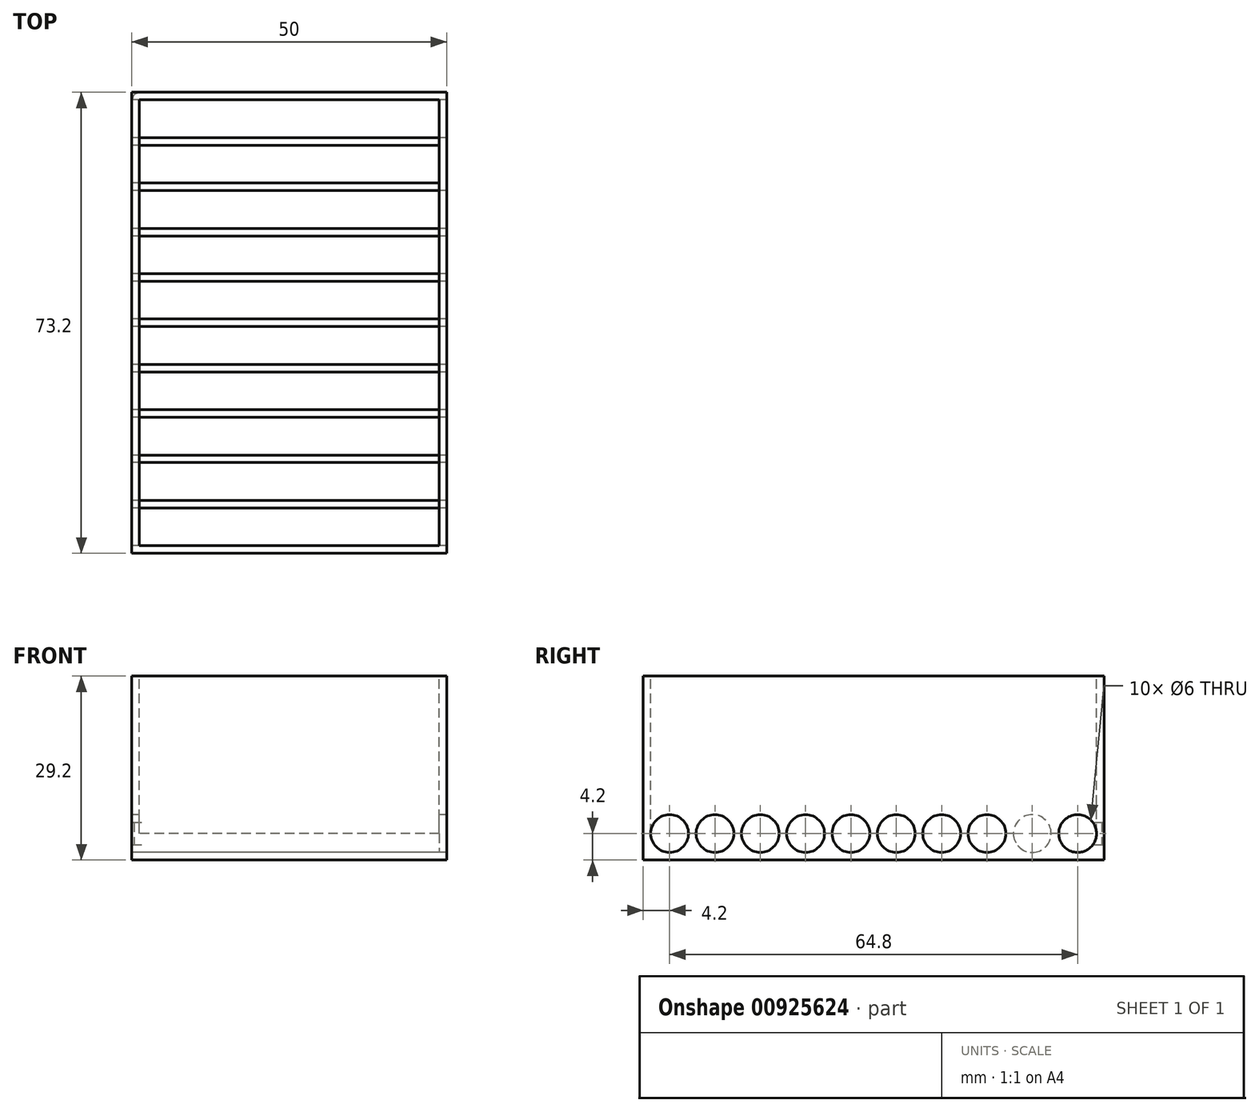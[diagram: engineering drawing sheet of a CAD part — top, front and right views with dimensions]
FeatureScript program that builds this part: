
annotation { "Feature Type Name" : "Feature", "Feature Type Description" : "" }
export const myFeature = defineFeature(function(context is Context, id is Id, definition is map)
    precondition{}
    {
        {
            assignVariable(context, id + "F0", {"name" : "FuseLength", "anyValue" : 20});
        }
        {
            var Q0;
            Q0=qCreatedBy(makeId("Right.planeOp"),FACE);
            var sketch = newSketch(context, id + "F1", { "sketchPlane" : qUnion([Q0])});
            skCircle(sketch, "E0", {"center": v(0, 3) * mm, "radius": 3 * mm});
            skCircle(sketch, "E1.1.0.0", {"center": v(7.2, 3) * mm, "radius": 3 * mm});
            skCircle(sketch, "E1.2.0.0", {"center": v(14.4, 3) * mm, "radius": 3 * mm});
            skCircle(sketch, "E1.3.0.0", {"center": v(21.6, 3) * mm, "radius": 3 * mm});
            skCircle(sketch, "E1.4.0.0", {"center": v(28.8, 3) * mm, "radius": 3 * mm});
            skCircle(sketch, "E1.5.0.0", {"center": v(36, 3) * mm, "radius": 3 * mm});
            skCircle(sketch, "E1.6.0.0", {"center": v(43.2, 3) * mm, "radius": 3 * mm});
            skCircle(sketch, "E1.7.0.0", {"center": v(50.4, 3) * mm, "radius": 3 * mm});
            skCircle(sketch, "E1.8.0.0", {"center": v(57.6, 3) * mm, "radius": 3 * mm});
            skCircle(sketch, "E1.9.0.0", {"center": v(64.8, 3) * mm, "radius": 3 * mm});
            skLineSegment(sketch, "E1.direction1", {"start": v(0, 3) * mm, "end": v(7.2, 3) * mm, "construction": true});
            skLineSegment(sketch, "E2", {"start": v(69, 3) * mm, "end": v(-4.2, 3) * mm});
            skLineSegment(sketch, "E3", {"start": v(-4.2, 3) * mm, "end": v(-4.2, -1.2) * mm});
            skLineSegment(sketch, "E4", {"start": v(-4.2, -1.2) * mm, "end": v(69, -1.2) * mm});
            skLineSegment(sketch, "E5", {"start": v(69, -1.2) * mm, "end": v(69, 3) * mm});
            skLineSegment(sketch, "E6.top", {"start": v(69, 28) * mm, "end": v(-4.2, 28) * mm});
            skLineSegment(sketch, "E6.left", {"start": v(69, 3) * mm, "end": v(69, 28) * mm});
            skLineSegment(sketch, "E6.right", {"start": v(-4.2, 3) * mm, "end": v(-4.2, 28) * mm});
            skSolve(sketch);
        }
        {
            var Q0;
            {var subQ0=sQuery(id+"F1.wireOp",EDGE,"E3");Q0=makeQuery(id+"F1.imprint","IMPRINT",FACE,{"disambiguationData":[TD([[makeQuery(id+"F1.imprint","IMPRINT",EDGE,{"derivedFrom":subQ0}),1.0]])]});}
            extrude(context, id + "F2", {"entities" : qUnion([Q0]), "depth" : (getVariable(context, 'FuseLength') * 2.5) * mm, "offsetDistance" : 25 * mm});
        }
        {
            var Q0;
            Q0=makeQuery(id+"F1.imprint","IMPRINT",FACE,{"disambiguationData":[TD([[makeQuery(id+"F1.imprint","IMPRINT",EDGE,{"derivedFrom":sQuery(id+"F1.wireOp",EDGE,"E6.top")}),1.0]])]});
            extrude(context, id + "F3", {"entities" : qUnion([Q0]), "operationType" : NewBodyOperationType.ADD, "depth" : 1.2 * mm, "offsetDistance" : 25 * mm});
        }
        {
            var Q0;
            Q0=makeQuery(id+"F2.opExtrude","CAP_FACE",FACE,{"disambiguationData":[OSD([sQuery(id+"F1.wireOp",EDGE,"E0"),sQuery(id+"F1.wireOp",EDGE,"E1.1.0.0"),sQuery(id+"F1.wireOp",EDGE,"E1.2.0.0"),sQuery(id+"F1.wireOp",EDGE,"E1.3.0.0"),sQuery(id+"F1.wireOp",EDGE,"E1.4.0.0"),sQuery(id+"F1.wireOp",EDGE,"E1.5.0.0"),sQuery(id+"F1.wireOp",EDGE,"E1.6.0.0"),sQuery(id+"F1.wireOp",EDGE,"E1.7.0.0"),sQuery(id+"F1.wireOp",EDGE,"E1.8.0.0"),sQuery(id+"F1.wireOp",EDGE,"E1.9.0.0"),sQuery(id+"F1.wireOp",EDGE,"E3"),sQuery(id+"F1.wireOp",EDGE,"E4"),sQuery(id+"F1.wireOp",EDGE,"E5"),sQuery(id+"F1.wireOp",EDGE,"E2")])],"isStart":false});
            var sketch = newSketch(context, id + "F4", { "sketchPlane" : qUnion([Q0])});
            skArc(sketch, "E7.0.0", {"start": v(54.6, 3) * mm, "mid": v(57.6, 6) * mm, "end": v(60.6, 3) * mm});
            skLineSegment(sketch, "E7.0.1", {"start": v(60.6, 3) * mm, "end": v(61.8, 3) * mm});
            skArc(sketch, "E7.0.2", {"start": v(61.8, 3) * mm, "mid": v(64.8, 6) * mm, "end": v(67.8, 3) * mm});
            skLineSegment(sketch, "E7.0.3", {"start": v(67.8, 3) * mm, "end": v(69, 3) * mm});
            skLineSegment(sketch, "E7.0.4", {"start": v(69, 3) * mm, "end": v(69, 28) * mm});
            skLineSegment(sketch, "E7.0.5", {"start": v(69, 28) * mm, "end": v(-4.2, 28) * mm});
            skLineSegment(sketch, "E7.0.6", {"start": v(-4.2, 28) * mm, "end": v(-4.2, 3) * mm});
            skLineSegment(sketch, "E7.0.7", {"start": v(-4.2, 3) * mm, "end": v(-3, 3) * mm});
            skArc(sketch, "E7.0.8", {"start": v(-3, 3) * mm, "mid": v(0, 6) * mm, "end": v(3, 3) * mm});
            skLineSegment(sketch, "E7.0.9", {"start": v(3, 3) * mm, "end": v(4.2, 3) * mm});
            skArc(sketch, "E7.0.10", {"start": v(4.2, 3) * mm, "mid": v(7.2, 6) * mm, "end": v(10.2, 3) * mm});
            skLineSegment(sketch, "E7.0.11", {"start": v(10.2, 3) * mm, "end": v(11.4, 3) * mm});
            skArc(sketch, "E7.0.12", {"start": v(11.4, 3) * mm, "mid": v(14.4, 6) * mm, "end": v(17.4, 3) * mm});
            skLineSegment(sketch, "E7.0.13", {"start": v(17.4, 3) * mm, "end": v(18.6, 3) * mm});
            skArc(sketch, "E7.0.14", {"start": v(18.6, 3) * mm, "mid": v(21.6, 6) * mm, "end": v(24.6, 3) * mm});
            skLineSegment(sketch, "E7.0.15", {"start": v(24.6, 3) * mm, "end": v(25.8, 3) * mm});
            skArc(sketch, "E7.0.16", {"start": v(25.8, 3) * mm, "mid": v(28.8, 6) * mm, "end": v(31.8, 3) * mm});
            skLineSegment(sketch, "E7.0.17", {"start": v(31.8, 3) * mm, "end": v(33, 3) * mm});
            skArc(sketch, "E7.0.18", {"start": v(33, 3) * mm, "mid": v(36, 6) * mm, "end": v(39, 3) * mm});
            skLineSegment(sketch, "E7.0.19", {"start": v(39, 3) * mm, "end": v(40.2, 3) * mm});
            skArc(sketch, "E7.0.20", {"start": v(40.2, 3) * mm, "mid": v(43.2, 6) * mm, "end": v(46.2, 3) * mm});
            skLineSegment(sketch, "E7.0.21", {"start": v(46.2, 3) * mm, "end": v(47.4, 3) * mm});
            skArc(sketch, "E7.0.22", {"start": v(47.4, 3) * mm, "mid": v(50.4, 6) * mm, "end": v(53.4, 3) * mm});
            skLineSegment(sketch, "E7.0.23", {"start": v(53.4, 3) * mm, "end": v(54.6, 3) * mm});
            skSolve(sketch);
        }
        {
            var Q0;
            Q0=makeQuery(id+"F4.imprint","IMPRINT",FACE,{"disambiguationData":[TD([[makeQuery(id+"F4.imprint","IMPRINT",EDGE,{"derivedFrom":sQuery(id+"F4.wireOp",EDGE,"E7.0.0")}),1.0]])]});
            var Q1;
            Q1=makeQuery(id+"F4.imprint","IMPRINT",FACE,{"disambiguationData":[TD([[makeQuery(id+"F4.imprint","IMPRINT",EDGE,{"derivedFrom":sQuery(id+"F4.wireOp",EDGE,"E7.0.10")}),-1.0]])]});
            var Q2;
            Q2=makeQuery(id+"F4.imprint","IMPRINT",FACE,{"disambiguationData":[TD([[makeQuery(id+"F4.imprint","IMPRINT",EDGE,{"derivedFrom":sQuery(id+"F4.wireOp",EDGE,"E7.0.12")}),-1.0]])]});
            var Q3;
            Q3=makeQuery(id+"F4.imprint","IMPRINT",FACE,{"disambiguationData":[TD([[makeQuery(id+"F4.imprint","IMPRINT",EDGE,{"derivedFrom":sQuery(id+"F4.wireOp",EDGE,"E7.0.14")}),-1.0]])]});
            var Q4;
            Q4=makeQuery(id+"F4.imprint","IMPRINT",FACE,{"disambiguationData":[TD([[makeQuery(id+"F4.imprint","IMPRINT",EDGE,{"derivedFrom":sQuery(id+"F4.wireOp",EDGE,"E7.0.16")}),-1.0]])]});
            var Q5;
            Q5=makeQuery(id+"F4.imprint","IMPRINT",FACE,{"disambiguationData":[TD([[makeQuery(id+"F4.imprint","IMPRINT",EDGE,{"derivedFrom":sQuery(id+"F4.wireOp",EDGE,"E7.0.18")}),-1.0]])]});
            var Q6;
            Q6=makeQuery(id+"F4.imprint","IMPRINT",FACE,{"disambiguationData":[TD([[makeQuery(id+"F4.imprint","IMPRINT",EDGE,{"derivedFrom":sQuery(id+"F4.wireOp",EDGE,"E7.0.20")}),-1.0]])]});
            var Q7;
            Q7=makeQuery(id+"F4.imprint","IMPRINT",FACE,{"disambiguationData":[TD([[makeQuery(id+"F4.imprint","IMPRINT",EDGE,{"derivedFrom":sQuery(id+"F4.wireOp",EDGE,"E7.0.22")}),-1.0]])]});
            var Q8;
            Q8=makeQuery(id+"F4.imprint","IMPRINT",FACE,{"disambiguationData":[TD([[makeQuery(id+"F4.imprint","IMPRINT",EDGE,{"derivedFrom":sQuery(id+"F4.wireOp",EDGE,"E7.0.0")}),-1.0]])]});
            var Q9;
            Q9=makeQuery(id+"F4.imprint","IMPRINT",FACE,{"disambiguationData":[TD([[makeQuery(id+"F4.imprint","IMPRINT",EDGE,{"derivedFrom":sQuery(id+"F4.wireOp",EDGE,"E7.0.2")}),-1.0]])]});
            var Q10;
            Q10=makeQuery(id+"F4.imprint","IMPRINT",FACE,{"disambiguationData":[TD([[makeQuery(id+"F4.imprint","IMPRINT",EDGE,{"derivedFrom":sQuery(id+"F4.wireOp",EDGE,"E7.0.8")}),-1.0]])]});
            extrude(context, id + "F5", {"entities" : qUnion([Q0, Q1, Q2, Q3, Q4, Q5, Q6, Q7, Q8, Q9, Q10]), "operationType" : NewBodyOperationType.ADD, "oppositeDirection" : true, "depth" : 1.2 * mm, "offsetDistance" : 25 * mm});
        }
        {
            var Q0;
            Q0=makeQuery(id+"F5.opExtrude","SWEPT_FACE",FACE,{"disambiguationData":[OSD([sQuery(id+"F4.wireOp",EDGE,"E7.0.5")])]});
            var sketch = newSketch(context, id + "F6", { "sketchPlane" : qUnion([Q0])});
            skLineSegment(sketch, "E8.bottom", {"start": v(1.2, 69) * mm, "end": v(48.8, 69) * mm});
            skLineSegment(sketch, "E8.top", {"start": v(1.2, 67.8) * mm, "end": v(48.8, 67.8) * mm});
            skLineSegment(sketch, "E8.left", {"start": v(1.2, 69) * mm, "end": v(1.2, 67.8) * mm});
            skLineSegment(sketch, "E8.right", {"start": v(48.8, 69) * mm, "end": v(48.8, 67.8) * mm});
            skLineSegment(sketch, "E9.bottom", {"start": v(1.2, -3) * mm, "end": v(48.8, -3) * mm});
            skLineSegment(sketch, "E9.top", {"start": v(1.2, -4.2) * mm, "end": v(48.8, -4.2) * mm});
            skLineSegment(sketch, "E9.left", {"start": v(1.2, -3) * mm, "end": v(1.2, -4.2) * mm});
            skLineSegment(sketch, "E9.right", {"start": v(48.8, -3) * mm, "end": v(48.8, -4.2) * mm});
            skSolve(sketch);
        }
        {
            var Q0;
            Q0=makeQuery(id+"F6.imprint","IMPRINT",FACE,{"disambiguationData":[TD([[makeQuery(id+"F6.imprint","IMPRINT",EDGE,{"derivedFrom":sQuery(id+"F6.wireOp",EDGE,"E9.bottom")}),-1.0]])]});
            var Q1;
            Q1=makeQuery(id+"F6.imprint","IMPRINT",FACE,{"disambiguationData":[TD([[makeQuery(id+"F6.imprint","IMPRINT",EDGE,{"derivedFrom":sQuery(id+"F6.wireOp",EDGE,"E8.bottom")}),-1.0]])]});
            extrude(context, id + "F7", {"entities" : qUnion([Q0, Q1]), "operationType" : NewBodyOperationType.ADD, "endBound" : BoundingType.UP_TO_NEXT, "oppositeDirection" : true, "depth" : 25 * mm, "offsetDistance" : 25 * mm});
        }
        {
            var Q0;
            Q0=makeQuery(id+"F3.boolean.opBoolean","MERGE",EDGE,{"derivedFrom":[makeQuery(id+"F2.opExtrude","CAP_EDGE",EDGE,{"disambiguationData":[OSD([sQuery(id+"F1.wireOp",EDGE,"E5")])],"isStart":true}),makeQuery(id+"F3.opExtrude","CAP_EDGE",EDGE,{"disambiguationData":[OSD([sQuery(id+"F1.wireOp",EDGE,"E6.left")])],"isStart":true})]});
            cPlane(context, id + "F8", {"entities" : qUnion([Q0]), "cplaneType" : CPlaneType.LINE_ANGLE, "offset" : 25 * mm, "angle" : 45 * degree, "width" : 150 * mm, "height" : 150 * mm});
        }
        {
            var Q0;
            Q0=qCreatedBy(id+"F8.planeOp",FACE);
            var sketch = newSketch(context, id + "F9", { "sketchPlane" : qUnion([Q0])});
            skLineSegment(sketch, "E10.bottom", {"start": v(49.29, 4.75) * mm, "end": v(48.3, 4.75) * mm});
            skLineSegment(sketch, "E10.top", {"start": v(49.29, 1.25) * mm, "end": v(48.3, 1.25) * mm});
            skLineSegment(sketch, "E10.left", {"start": v(48.3, 4.75) * mm, "end": v(48.3, 1.25) * mm});
            skLineSegment(sketch, "E10.right", {"start": v(49.29, 4.75) * mm, "end": v(49.29, 1.25) * mm});
            skPoint(sketch, "E11", {"position": v(49.29, 3) * mm});
            skPoint(sketch, "E12", {"position": v(48.8, 4.75) * mm});
            skSolve(sketch);
        }
        {
            var Q0;
            Q0=makeQuery(id+"F9.imprint","IMPRINT",FACE,{"disambiguationData":[TD([[makeQuery(id+"F9.imprint","IMPRINT",EDGE,{"derivedFrom":sQuery(id+"F9.wireOp",EDGE,"E10.bottom")}),1.0]])]});
            extrude(context, id + "F10", {"entities" : qUnion([Q0]), "operationType" : NewBodyOperationType.REMOVE, "endBound" : BoundingType.THROUGH_ALL, "depth" : 25 * mm, "offsetDistance" : 25 * mm, "hasSecondDirection" : true, "secondDirectionBound" : SecondDirectionBoundingType.THROUGH_ALL, "secondDirectionOppositeDirection" : true, "secondDirectionDepth" : 25 * mm});
        }
        {
            var Q0;
            {var subQ0=sQuery(id+"F1.wireOp",EDGE,"E2");var subQ1=sQuery(id+"F1.wireOp",EDGE,"E1.9.0.0");var subQ2=sQuery(id+"F1.wireOp",EDGE,"E1.8.0.0");var subQ3=sQuery(id+"F1.wireOp",EDGE,"E1.7.0.0");var subQ4=sQuery(id+"F1.wireOp",EDGE,"E1.6.0.0");var subQ5=sQuery(id+"F1.wireOp",EDGE,"E1.5.0.0");var subQ6=sQuery(id+"F1.wireOp",EDGE,"E1.4.0.0");var subQ7=sQuery(id+"F1.wireOp",EDGE,"E1.3.0.0");var subQ8=sQuery(id+"F1.wireOp",EDGE,"E1.2.0.0");var subQ9=sQuery(id+"F1.wireOp",EDGE,"E1.1.0.0");var subQ10=sQuery(id+"F1.wireOp",EDGE,"E0");Q0=makeQuery(id+"F3.boolean.opBoolean","MERGE",FACE,{"derivedFrom":[makeQuery(id+"F2.opExtrude","CAP_FACE",FACE,{"disambiguationData":[OSD([subQ10,subQ9,subQ8,subQ7,subQ6,subQ5,subQ4,subQ3,subQ2,subQ1,sQuery(id+"F1.wireOp",EDGE,"E3"),sQuery(id+"F1.wireOp",EDGE,"E4"),sQuery(id+"F1.wireOp",EDGE,"E5"),subQ0])],"isStart":true}),makeQuery(id+"F3.opExtrude","CAP_FACE",FACE,{"disambiguationData":[OSD([subQ10,subQ9,subQ8,subQ7,subQ6,subQ5,subQ4,subQ3,subQ2,subQ1,subQ0,sQuery(id+"F1.wireOp",EDGE,"E6.top"),sQuery(id+"F1.wireOp",EDGE,"E6.left"),sQuery(id+"F1.wireOp",EDGE,"E6.right")])],"isStart":true})]});}
            var sketch = newSketch(context, id + "F11", { "sketchPlane" : qUnion([Q0])});
            skLineSegment(sketch, "E13", {"start": v(-32.4, 28) * mm, "end": v(-32.4, -1.2) * mm});
            skSolve(sketch);
        }
        {
            var Q0;
            Q0=sQuery(id+"F11.wireOp",EDGE,"E13");
            cPlane(context, id + "F12", {"entities" : qUnion([Q0]), "cplaneType" : CPlaneType.LINE_ANGLE, "offset" : 25 * mm, "angle" : 90 * degree, "oppositeDirection" : true, "width" : 150 * mm, "height" : 150 * mm});
        }
        {
            var Q0;
            Q0=makeQuery(id+"FdSzlUw70HAmy3g_1.1.F10.boolean.opBoolean","INTERSECT",EDGE,{"derivedFrom":[makeQuery(id+"F7.boolean.opBoolean","MERGE",FACE,{"derivedFrom":[makeQuery(id+"F5.boolean.opBoolean","MERGE",FACE,{"derivedFrom":[makeQuery(id+"F3.boolean.opBoolean","MERGE",FACE,{"derivedFrom":[makeQuery(id+"F2.opExtrude","SWEPT_FACE",FACE,{"disambiguationData":[OSD([sQuery(id+"F1.wireOp",EDGE,"E3")])]}),makeQuery(id+"F3.opExtrude","SWEPT_FACE",FACE,{"disambiguationData":[OSD([sQuery(id+"F1.wireOp",EDGE,"E6.right")])]})]}),makeQuery(id+"F5.opExtrude","SWEPT_FACE",FACE,{"disambiguationData":[OSD([sQuery(id+"F4.wireOp",EDGE,"E7.0.6")])]})]}),makeQuery(id+"F7.opExtrude","SWEPT_FACE",FACE,{"disambiguationData":[OSD([sQuery(id+"F6.wireOp",EDGE,"E9.top")])]})]}),makeQuery(id+"FdSzlUw70HAmy3g_1.1.F10.opExtrude","SWEPT_FACE",FACE,{"disambiguationData":[OSD([sQuery(id+"F9.wireOp",EDGE,"E10.left")])]})]});
            var Q1;
            {var subQ0=sQuery(id+"F1.wireOp",EDGE,"E2");var subQ1=sQuery(id+"F1.wireOp",EDGE,"E1.9.0.0");var subQ2=sQuery(id+"F1.wireOp",EDGE,"E1.8.0.0");var subQ3=sQuery(id+"F1.wireOp",EDGE,"E1.7.0.0");var subQ4=sQuery(id+"F1.wireOp",EDGE,"E1.6.0.0");var subQ5=sQuery(id+"F1.wireOp",EDGE,"E1.5.0.0");var subQ6=sQuery(id+"F1.wireOp",EDGE,"E1.4.0.0");var subQ7=sQuery(id+"F1.wireOp",EDGE,"E1.3.0.0");var subQ8=sQuery(id+"F1.wireOp",EDGE,"E1.2.0.0");var subQ9=sQuery(id+"F1.wireOp",EDGE,"E1.1.0.0");var subQ10=sQuery(id+"F1.wireOp",EDGE,"E0");Q1=makeQuery(id+"FdSzlUw70HAmy3g_1.1.F10.boolean.opBoolean","INTERSECT",EDGE,{"derivedFrom":[makeQuery(id+"F3.boolean.opBoolean","MERGE",FACE,{"derivedFrom":[makeQuery(id+"F2.opExtrude","CAP_FACE",FACE,{"disambiguationData":[OSD([subQ10,subQ9,subQ8,subQ7,subQ6,subQ5,subQ4,subQ3,subQ2,subQ1,sQuery(id+"F1.wireOp",EDGE,"E3"),sQuery(id+"F1.wireOp",EDGE,"E4"),sQuery(id+"F1.wireOp",EDGE,"E5"),subQ0])],"isStart":true}),makeQuery(id+"F3.opExtrude","CAP_FACE",FACE,{"disambiguationData":[OSD([subQ10,subQ9,subQ8,subQ7,subQ6,subQ5,subQ4,subQ3,subQ2,subQ1,subQ0,sQuery(id+"F1.wireOp",EDGE,"E6.top"),sQuery(id+"F1.wireOp",EDGE,"E6.left"),sQuery(id+"F1.wireOp",EDGE,"E6.right")])],"isStart":true})]}),makeQuery(id+"FdSzlUw70HAmy3g_1.1.F10.opExtrude","SWEPT_FACE",FACE,{"disambiguationData":[OSD([sQuery(id+"F9.wireOp",EDGE,"E10.left")])]})]});}
            var Q2;
            {var subQ0=sQuery(id+"F1.wireOp",EDGE,"E2");var subQ1=sQuery(id+"F1.wireOp",EDGE,"E1.9.0.0");var subQ2=sQuery(id+"F1.wireOp",EDGE,"E1.8.0.0");var subQ3=sQuery(id+"F1.wireOp",EDGE,"E1.7.0.0");var subQ4=sQuery(id+"F1.wireOp",EDGE,"E1.6.0.0");var subQ5=sQuery(id+"F1.wireOp",EDGE,"E1.5.0.0");var subQ6=sQuery(id+"F1.wireOp",EDGE,"E1.4.0.0");var subQ7=sQuery(id+"F1.wireOp",EDGE,"E1.3.0.0");var subQ8=sQuery(id+"F1.wireOp",EDGE,"E1.2.0.0");var subQ9=sQuery(id+"F1.wireOp",EDGE,"E1.1.0.0");var subQ10=sQuery(id+"F1.wireOp",EDGE,"E0");Q2=makeQuery(id+"F10.boolean.opBoolean","INTERSECT",EDGE,{"derivedFrom":[makeQuery(id+"F3.boolean.opBoolean","MERGE",FACE,{"derivedFrom":[makeQuery(id+"F2.opExtrude","CAP_FACE",FACE,{"disambiguationData":[OSD([subQ10,subQ9,subQ8,subQ7,subQ6,subQ5,subQ4,subQ3,subQ2,subQ1,sQuery(id+"F1.wireOp",EDGE,"E3"),sQuery(id+"F1.wireOp",EDGE,"E4"),sQuery(id+"F1.wireOp",EDGE,"E5"),subQ0])],"isStart":true}),makeQuery(id+"F3.opExtrude","CAP_FACE",FACE,{"disambiguationData":[OSD([subQ10,subQ9,subQ8,subQ7,subQ6,subQ5,subQ4,subQ3,subQ2,subQ1,subQ0,sQuery(id+"F1.wireOp",EDGE,"E6.top"),sQuery(id+"F1.wireOp",EDGE,"E6.left"),sQuery(id+"F1.wireOp",EDGE,"E6.right")])],"isStart":true})]}),makeQuery(id+"F10.opExtrude","SWEPT_FACE",FACE,{"disambiguationData":[OSD([sQuery(id+"F9.wireOp",EDGE,"E10.left")])]})]});}
            var Q3;
            Q3=makeQuery(id+"F10.boolean.opBoolean","INTERSECT",EDGE,{"derivedFrom":[makeQuery(id+"F7.boolean.opBoolean","MERGE",FACE,{"derivedFrom":[makeQuery(id+"F5.boolean.opBoolean","MERGE",FACE,{"derivedFrom":[makeQuery(id+"F3.boolean.opBoolean","MERGE",FACE,{"derivedFrom":[makeQuery(id+"F2.opExtrude","SWEPT_FACE",FACE,{"disambiguationData":[OSD([sQuery(id+"F1.wireOp",EDGE,"E5")])]}),makeQuery(id+"F3.opExtrude","SWEPT_FACE",FACE,{"disambiguationData":[OSD([sQuery(id+"F1.wireOp",EDGE,"E6.left")])]})]}),makeQuery(id+"F5.opExtrude","SWEPT_FACE",FACE,{"disambiguationData":[OSD([sQuery(id+"F4.wireOp",EDGE,"E7.0.4")])]})]}),makeQuery(id+"F7.opExtrude","SWEPT_FACE",FACE,{"disambiguationData":[OSD([sQuery(id+"F6.wireOp",EDGE,"E8.bottom")])]})]}),makeQuery(id+"F10.opExtrude","SWEPT_FACE",FACE,{"disambiguationData":[OSD([sQuery(id+"F9.wireOp",EDGE,"E10.left")])]})]});
            fillet(context, id + "F13", {"entities" : qUnion([Q0, Q1, Q2, Q3]), "radius" : 2 * mm, "tangentPropagation" : true, "allowEdgeOverflow" : false});
        }
    });
